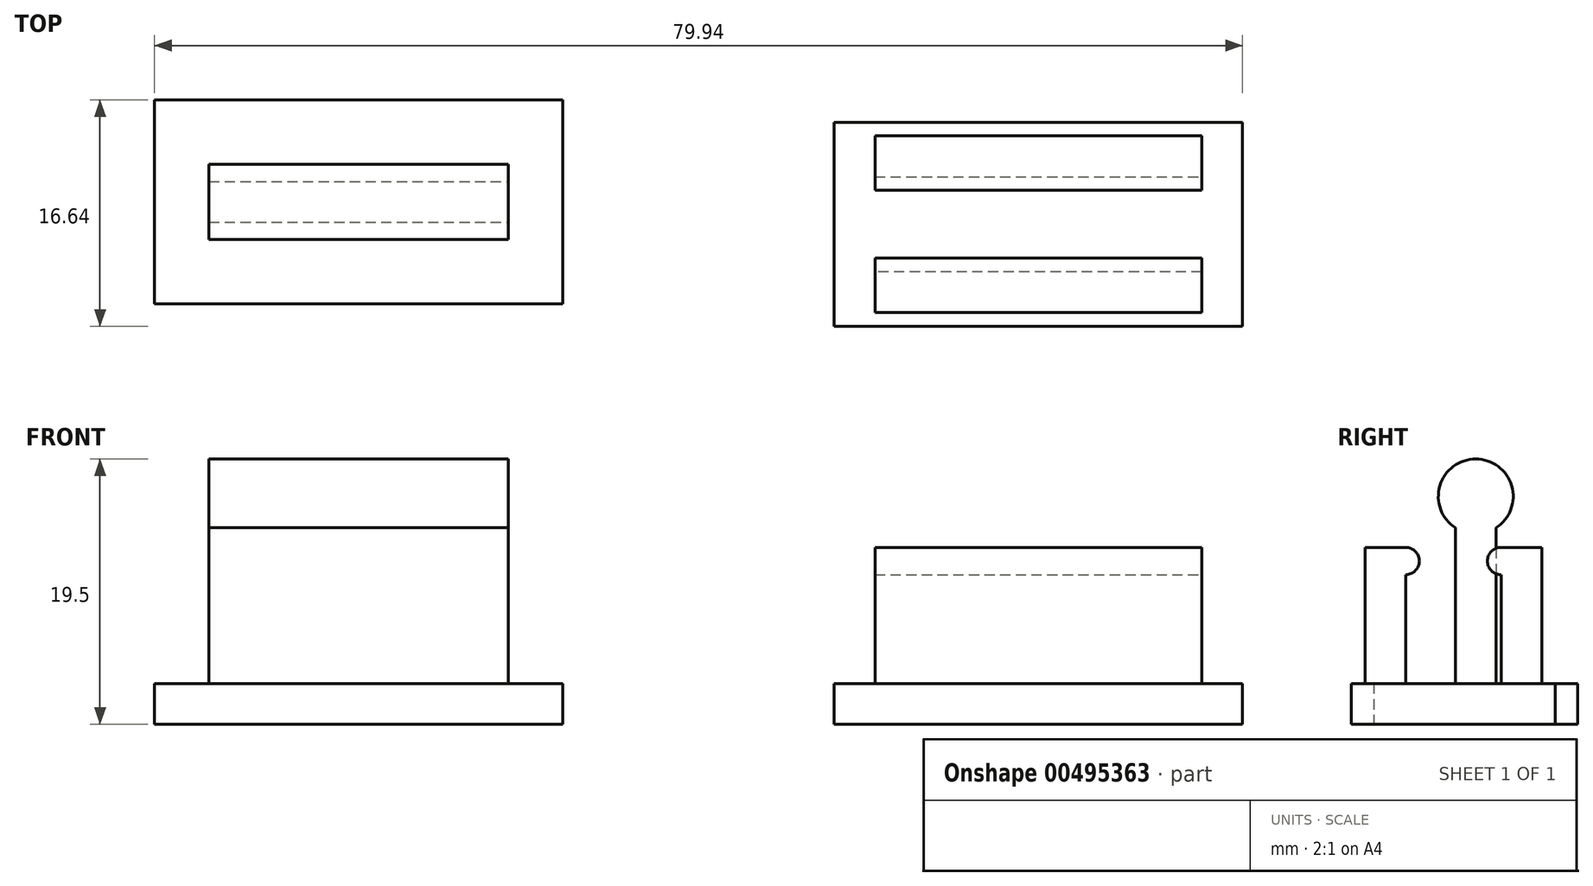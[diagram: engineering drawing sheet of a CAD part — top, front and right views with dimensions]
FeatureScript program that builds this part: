
annotation { "Feature Type Name" : "Feature", "Feature Type Description" : "" }
export const myFeature = defineFeature(function(context is Context, id is Id, definition is map)
    precondition{}
    {
        {
            var Q0;
            Q0=qCreatedBy(makeId("Top.planeOp"),FACE);
            var sketch = newSketch(context, id + "F0", { "sketchPlane" : qUnion([Q0])});
            skLineSegment(sketch, "E0.bottom", {"start": v(-44.7, -7.92) * mm, "end": v(-14.7, -7.92) * mm});
            skLineSegment(sketch, "E0.top", {"start": v(-44.7, 7.08) * mm, "end": v(-14.7, 7.08) * mm});
            skLineSegment(sketch, "E0.left", {"start": v(-44.7, -7.92) * mm, "end": v(-44.7, 7.08) * mm});
            skLineSegment(sketch, "E0.right", {"start": v(-14.7, -7.92) * mm, "end": v(-14.7, 7.08) * mm});
            skLineSegment(sketch, "E1.bottom", {"start": v(5.24, 5.44) * mm, "end": v(35.24, 5.44) * mm});
            skLineSegment(sketch, "E1.top", {"start": v(5.24, -9.56) * mm, "end": v(35.24, -9.56) * mm});
            skLineSegment(sketch, "E1.left", {"start": v(5.24, 5.44) * mm, "end": v(5.24, -9.56) * mm});
            skLineSegment(sketch, "E1.right", {"start": v(35.24, 5.44) * mm, "end": v(35.24, -9.56) * mm});
            skSolve(sketch);
        }
        {
            var Q0;
            Q0 = qSketchRegion(id + "F0", true);
            extrude(context, id + "F1", {"entities" : qUnion([Q0]), "depth" : 3 * mm});
        }
        {
            var Q0;
            Q0=makeQuery(id+"F1.opExtrude","CAP_FACE",FACE,{"disambiguationData":[OSD([sQuery(id+"F0.wireOp",EDGE,"E1.bottom"),sQuery(id+"F0.wireOp",EDGE,"E1.top"),sQuery(id+"F0.wireOp",EDGE,"E1.left"),sQuery(id+"F0.wireOp",EDGE,"E1.right")])],"isStart":false});
            var sketch = newSketch(context, id + "F2", { "sketchPlane" : qUnion([Q0])});
            skLineSegment(sketch, "E2.bottom", {"start": v(8.24, 1.44) * mm, "end": v(32.24, 1.44) * mm});
            skLineSegment(sketch, "E2.top", {"start": v(8.24, 4.44) * mm, "end": v(32.24, 4.44) * mm});
            skLineSegment(sketch, "E2.left", {"start": v(8.24, 1.44) * mm, "end": v(8.24, 4.44) * mm});
            skLineSegment(sketch, "E2.right", {"start": v(32.24, 1.44) * mm, "end": v(32.24, 4.44) * mm});
            skLineSegment(sketch, "E3.bottom", {"start": v(32.24, -5.56) * mm, "end": v(8.24, -5.56) * mm});
            skLineSegment(sketch, "E3.top", {"start": v(32.24, -8.56) * mm, "end": v(8.24, -8.56) * mm});
            skLineSegment(sketch, "E3.left", {"start": v(32.24, -5.56) * mm, "end": v(32.24, -8.56) * mm});
            skLineSegment(sketch, "E3.right", {"start": v(8.24, -5.56) * mm, "end": v(8.24, -8.56) * mm});
            skSolve(sketch);
        }
        {
            var Q0;
            Q0 = qSketchRegion(id + "F2", true);
            extrude(context, id + "F3", {"entities" : qUnion([Q0]), "operationType" : NewBodyOperationType.ADD, "depth" : 10 * mm});
        }
        {
            var Q0;
            Q0=makeQuery(id+"F3.opExtrude","SWEPT_FACE",FACE,{"disambiguationData":[OSD([sQuery(id+"F2.wireOp",EDGE,"E3.left")])]});
            var sketch = newSketch(context, id + "F4", { "sketchPlane" : qUnion([Q0])});
            skCircle(sketch, "E4", {"center": v(-5.56, 12) * mm, "radius": 1 * mm});
            skSolve(sketch);
        }
        {
            var Q0;
            Q0 = qSketchRegion(id + "F4", true);
            extrude(context, id + "F5", {"entities" : qUnion([Q0]), "operationType" : NewBodyOperationType.ADD, "oppositeDirection" : true, "depth" : 24 * mm});
        }
        {
            var Q0;
            Q0=makeQuery(id+"F3.opExtrude","SWEPT_FACE",FACE,{"disambiguationData":[OSD([sQuery(id+"F2.wireOp",EDGE,"E2.right")])]});
            var sketch = newSketch(context, id + "F6", { "sketchPlane" : qUnion([Q0])});
            skCircle(sketch, "E5", {"center": v(1.44, 12) * mm, "radius": 1 * mm});
            skSolve(sketch);
        }
        {
            var Q0;
            Q0 = qSketchRegion(id + "F6", true);
            extrude(context, id + "F7", {"entities" : qUnion([Q0]), "operationType" : NewBodyOperationType.ADD, "oppositeDirection" : true, "depth" : 24 * mm});
        }
        {
            var Q0;
            Q0=makeQuery(id+"F1.opExtrude","CAP_FACE",FACE,{"disambiguationData":[OSD([sQuery(id+"F0.wireOp",EDGE,"E0.bottom"),sQuery(id+"F0.wireOp",EDGE,"E0.top"),sQuery(id+"F0.wireOp",EDGE,"E0.left"),sQuery(id+"F0.wireOp",EDGE,"E0.right")])],"isStart":false});
            var sketch = newSketch(context, id + "F8", { "sketchPlane" : qUnion([Q0])});
            skLineSegment(sketch, "E6.bottom", {"start": v(-40.7, -1.92) * mm, "end": v(-18.7, -1.92) * mm});
            skLineSegment(sketch, "E6.top", {"start": v(-40.7, 1.08) * mm, "end": v(-18.7, 1.08) * mm});
            skLineSegment(sketch, "E6.left", {"start": v(-40.7, -1.92) * mm, "end": v(-40.7, 1.08) * mm});
            skLineSegment(sketch, "E6.right", {"start": v(-18.7, -1.92) * mm, "end": v(-18.7, 1.08) * mm});
            skSolve(sketch);
        }
        {
            var Q0;
            Q0 = qSketchRegion(id + "F8", true);
            extrude(context, id + "F9", {"entities" : qUnion([Q0]), "operationType" : NewBodyOperationType.ADD, "depth" : 15 * mm});
        }
        {
            var Q0;
            Q0=makeQuery(id+"F9.opExtrude","SWEPT_FACE",FACE,{"disambiguationData":[OSD([sQuery(id+"F8.wireOp",EDGE,"E6.left")])]});
            var sketch = newSketch(context, id + "F10", { "sketchPlane" : qUnion([Q0])});
            skCircle(sketch, "E7", {"center": v(0.42, 16.75) * mm, "radius": 2.75 * mm});
            skSolve(sketch);
        }
        {
            var Q0;
            Q0 = qSketchRegion(id + "F10", true);
            extrude(context, id + "F11", {"entities" : qUnion([Q0]), "operationType" : NewBodyOperationType.ADD, "oppositeDirection" : true, "depth" : 22 * mm});
        }
    });
